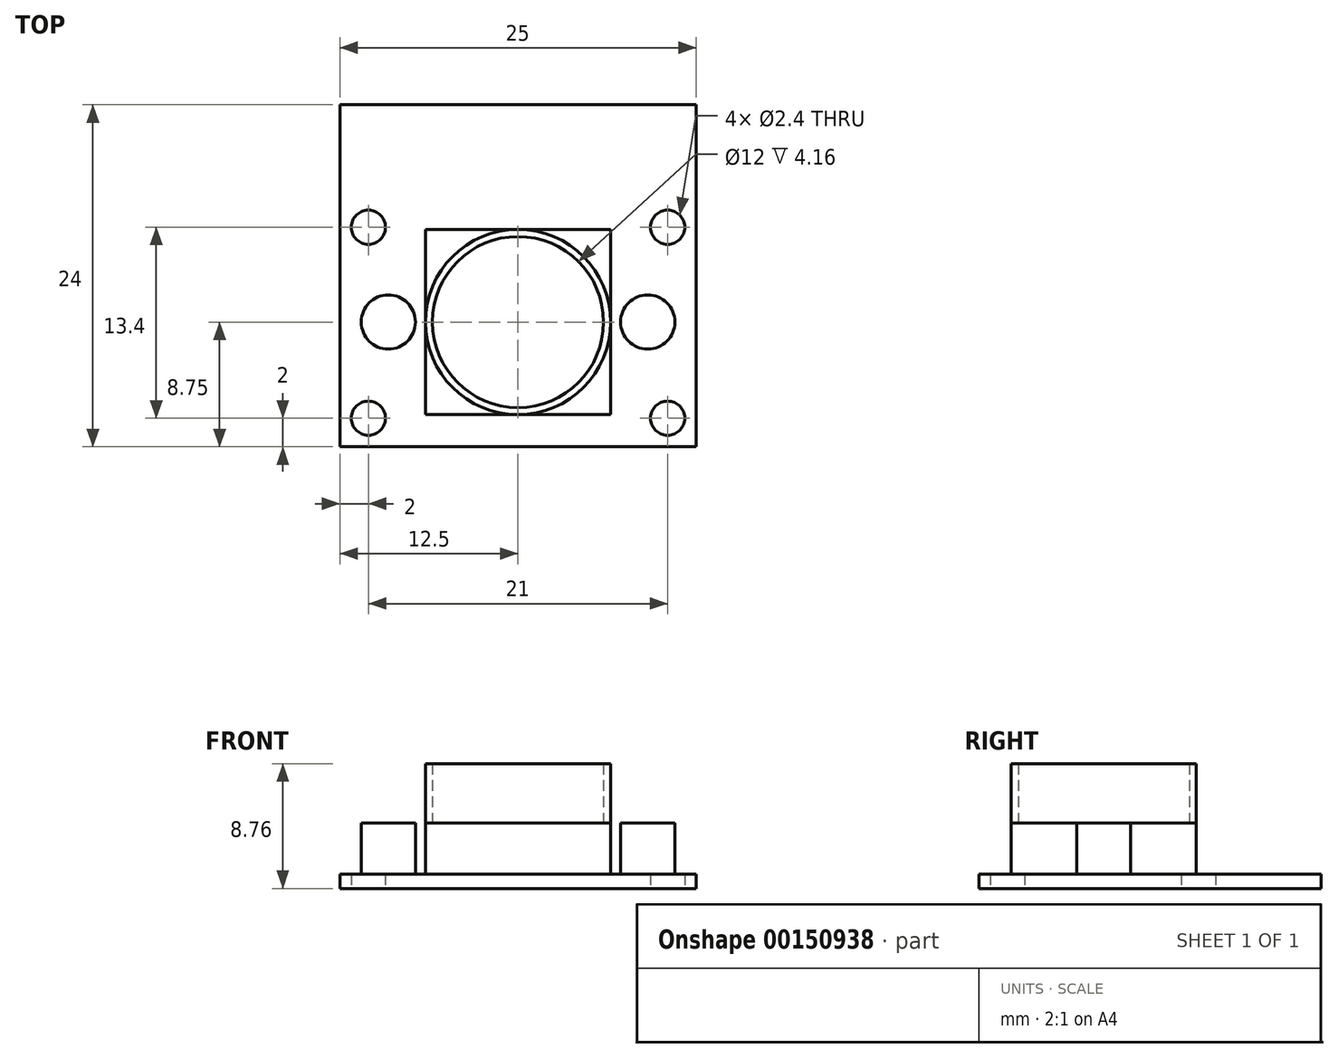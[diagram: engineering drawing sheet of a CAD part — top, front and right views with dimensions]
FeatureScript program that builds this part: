
annotation { "Feature Type Name" : "Feature", "Feature Type Description" : "" }
export const myFeature = defineFeature(function(context is Context, id is Id, definition is map)
    precondition{}
    {
        {
            var Q0;
            Q0=qCreatedBy(makeId("Top.planeOp"),FACE);
            var sketch = newSketch(context, id + "F0", { "sketchPlane" : qUnion([Q0])});
            skLineSegment(sketch, "E0.bottom", {"start": v(-12.5, 12) * mm, "end": v(12.5, 12) * mm});
            skLineSegment(sketch, "E0.top", {"start": v(-12.5, -12) * mm, "end": v(12.5, -12) * mm});
            skLineSegment(sketch, "E0.left", {"start": v(-12.5, 12) * mm, "end": v(-12.5, -12) * mm});
            skLineSegment(sketch, "E0.right", {"start": v(12.5, 12) * mm, "end": v(12.5, -12) * mm});
            skPoint(sketch, "E0.middle", {"position": v(0, 0) * mm});
            skCircle(sketch, "E1", {"center": v(-10.5, 3.4) * mm, "radius": 1.2 * mm});
            skCircle(sketch, "E2", {"center": v(10.5, 3.4) * mm, "radius": 1.2 * mm});
            skCircle(sketch, "E3", {"center": v(10.5, -10) * mm, "radius": 1.2 * mm});
            skCircle(sketch, "E4", {"center": v(-10.5, -10) * mm, "radius": 1.2 * mm});
            skPoint(sketch, "E5", {"position": v(0, -3.3) * mm});
            skLineSegment(sketch, "E6", {"start": v(-10.5, 2.2) * mm, "end": v(10.5, 2.2) * mm});
            skLineSegment(sketch, "E7", {"start": v(-10.5, -8.8) * mm, "end": v(10.5, -8.8) * mm});
            skSolve(sketch);
        }
        {
            var Q0;
            Q0=makeQuery(id+"F0.imprint","IMPRINT",FACE,{"disambiguationData":[TD([[makeQuery(id+"F0.imprint","IMPRINT",EDGE,{"derivedFrom":sQuery(id+"F0.wireOp",EDGE,"E0.bottom")}),-1.0]])]});
            extrude(context, id + "F1", {"entities" : qUnion([Q0]), "depth" : 1 * mm});
        }
        {
            var Q0;
            Q0=makeQuery(id+"F1.opExtrude","CAP_FACE",FACE,{"disambiguationData":[OSD([sQuery(id+"F0.wireOp",EDGE,"E0.bottom"),sQuery(id+"F0.wireOp",EDGE,"E0.top"),sQuery(id+"F0.wireOp",EDGE,"E0.left"),sQuery(id+"F0.wireOp",EDGE,"E0.right"),sQuery(id+"F0.wireOp",EDGE,"E1"),sQuery(id+"F0.wireOp",EDGE,"E2"),sQuery(id+"F0.wireOp",EDGE,"E3"),sQuery(id+"F0.wireOp",EDGE,"E4")])],"isStart":false});
            var sketch = newSketch(context, id + "F2", { "sketchPlane" : qUnion([Q0])});
            skLineSegment(sketch, "E8.bottom", {"start": v(-6.5, 3.25) * mm, "end": v(6.5, 3.25) * mm});
            skLineSegment(sketch, "E8.top", {"start": v(-6.5, -9.75) * mm, "end": v(6.5, -9.75) * mm});
            skLineSegment(sketch, "E8.left", {"start": v(-6.5, 3.25) * mm, "end": v(-6.5, -9.75) * mm});
            skLineSegment(sketch, "E8.right", {"start": v(6.5, 3.25) * mm, "end": v(6.5, -9.75) * mm});
            skPoint(sketch, "E8.middle", {"position": v(0, -3.25) * mm});
            skPoint(sketch, "E9.middle", {"position": v(6.5, -3.25) * mm});
            skPoint(sketch, "E10.middle", {"position": v(-6.5, -3.25) * mm});
            skLineSegment(sketch, "E11", {"start": v(6.5, -1.35) * mm, "end": v(6.5, -5.15) * mm});
            skLineSegment(sketch, "E12", {"start": v(-6.5, -1.35) * mm, "end": v(-6.5, -5.15) * mm});
            skCircle(sketch, "E13", {"center": v(-9.1, -3.25) * mm, "radius": 1.9 * mm});
            skLineSegment(sketch, "E14", {"start": v(-6.5, -1.35) * mm, "end": v(-9.1, -1.35) * mm});
            skLineSegment(sketch, "E15", {"start": v(-6.5, -5.15) * mm, "end": v(-9.1, -5.15) * mm});
            skCircle(sketch, "E16", {"center": v(9.1, -3.25) * mm, "radius": 1.9 * mm});
            skLineSegment(sketch, "E17", {"start": v(6.5, -5.15) * mm, "end": v(9.1, -5.15) * mm});
            skLineSegment(sketch, "E18", {"start": v(9.1, -1.35) * mm, "end": v(6.5, -1.35) * mm});
            skSolve(sketch);
        }
        {
            var Q0;
            {var subQ3=sQuery(id+"F2.wireOp",EDGE,"E8.bottom");Q0=makeQuery(id+"F2.imprint","IMPRINT",FACE,{"disambiguationData":[TD([[makeQuery(id+"F2.imprint","IMPRINT",EDGE,{"derivedFrom":subQ3}),-1.0]])]});}
            var Q1;
            Q1=makeQuery(id+"F2.imprint","IMPRINT",FACE,{"disambiguationData":[TD([[makeQuery(id+"F2.imprint","IMPRINT",EDGE,{"derivedFrom":sQuery(id+"F2.wireOp",EDGE,"E12")}),-1.0]])]});
            var Q2;
            {var subQ0=sQuery(id+"F2.wireOp",EDGE,"E13");var subQ1=makeQuery(id+"F2.imprint","INTERSECT",VERTEX,{"derivedFrom":[subQ0,sQuery(id+"F2.wireOp",EDGE,"E14")]});Q2=makeQuery(id+"F2.imprint","IMPRINT",FACE,{"disambiguationData":[TD([[makeQuery(id+"F2.imprint","IMPRINT",EDGE,{"disambiguationData":[TD([[subQ1,-1.0]])],"derivedFrom":subQ0}),1.0]])]});}
            var Q3;
            Q3=makeQuery(id+"F2.imprint","IMPRINT",FACE,{"disambiguationData":[TD([[makeQuery(id+"F2.imprint","IMPRINT",EDGE,{"derivedFrom":sQuery(id+"F2.wireOp",EDGE,"E11")}),1.0]])]});
            var Q4;
            {var subQ0=sQuery(id+"F2.wireOp",EDGE,"E16");var subQ1=makeQuery(id+"F2.imprint","INTERSECT",VERTEX,{"derivedFrom":[subQ0,sQuery(id+"F2.wireOp",EDGE,"E17")]});Q4=makeQuery(id+"F2.imprint","IMPRINT",FACE,{"disambiguationData":[TD([[makeQuery(id+"F2.imprint","IMPRINT",EDGE,{"disambiguationData":[TD([[subQ1,1.0]])],"derivedFrom":subQ0}),1.0]])]});}
            extrude(context, id + "F3", {"entities" : qUnion([Q0, Q1, Q2, Q3, Q4]), "operationType" : NewBodyOperationType.ADD, "depth" : 3.6 * mm});
        }
        {
            var Q0;
            Q0=makeQuery(id+"F3.opExtrude","CAP_FACE",FACE,{"disambiguationData":[OSD([sQuery(id+"F2.wireOp",EDGE,"E8.bottom"),sQuery(id+"F2.wireOp",EDGE,"E8.top"),sQuery(id+"F2.wireOp",EDGE,"E8.left"),sQuery(id+"F2.wireOp",EDGE,"E8.right"),sQuery(id+"F2.wireOp",EDGE,"E13"),sQuery(id+"F2.wireOp",EDGE,"E14"),sQuery(id+"F2.wireOp",EDGE,"E15"),sQuery(id+"F2.wireOp",EDGE,"E16"),sQuery(id+"F2.wireOp",EDGE,"E17"),sQuery(id+"F2.wireOp",EDGE,"E18")])],"isStart":false});
            var sketch = newSketch(context, id + "F4", { "sketchPlane" : qUnion([Q0])});
            skCircle(sketch, "E19", {"center": v(0, -3.25) * mm, "radius": 6.5 * mm});
            skPoint(sketch, "E19.first.point", {"position": v(0, 3.25) * mm});
            skPoint(sketch, "E19.second.point", {"position": v(0, -9.75) * mm});
            skPoint(sketch, "E19.third.point", {"position": v(6.5, -3.25) * mm});
            skPoint(sketch, "E19.third.point.positionSnap0", {"position": v(11, -3.25) * mm});
            skCircle(sketch, "E20", {"center": v(0, -3.25) * mm, "radius": 6 * mm});
            skSolve(sketch);
        }
        {
            var Q0;
            Q0=makeQuery(id+"F4.imprint","IMPRINT",FACE,{"disambiguationData":[TD([[makeQuery(id+"F4.imprint","IMPRINT",EDGE,{"derivedFrom":sQuery(id+"F4.wireOp",EDGE,"E20")}),-1.0]])]});
            extrude(context, id + "F5", {"entities" : qUnion([Q0]), "operationType" : NewBodyOperationType.ADD, "depth" : 4.16 * mm});
        }
    });
